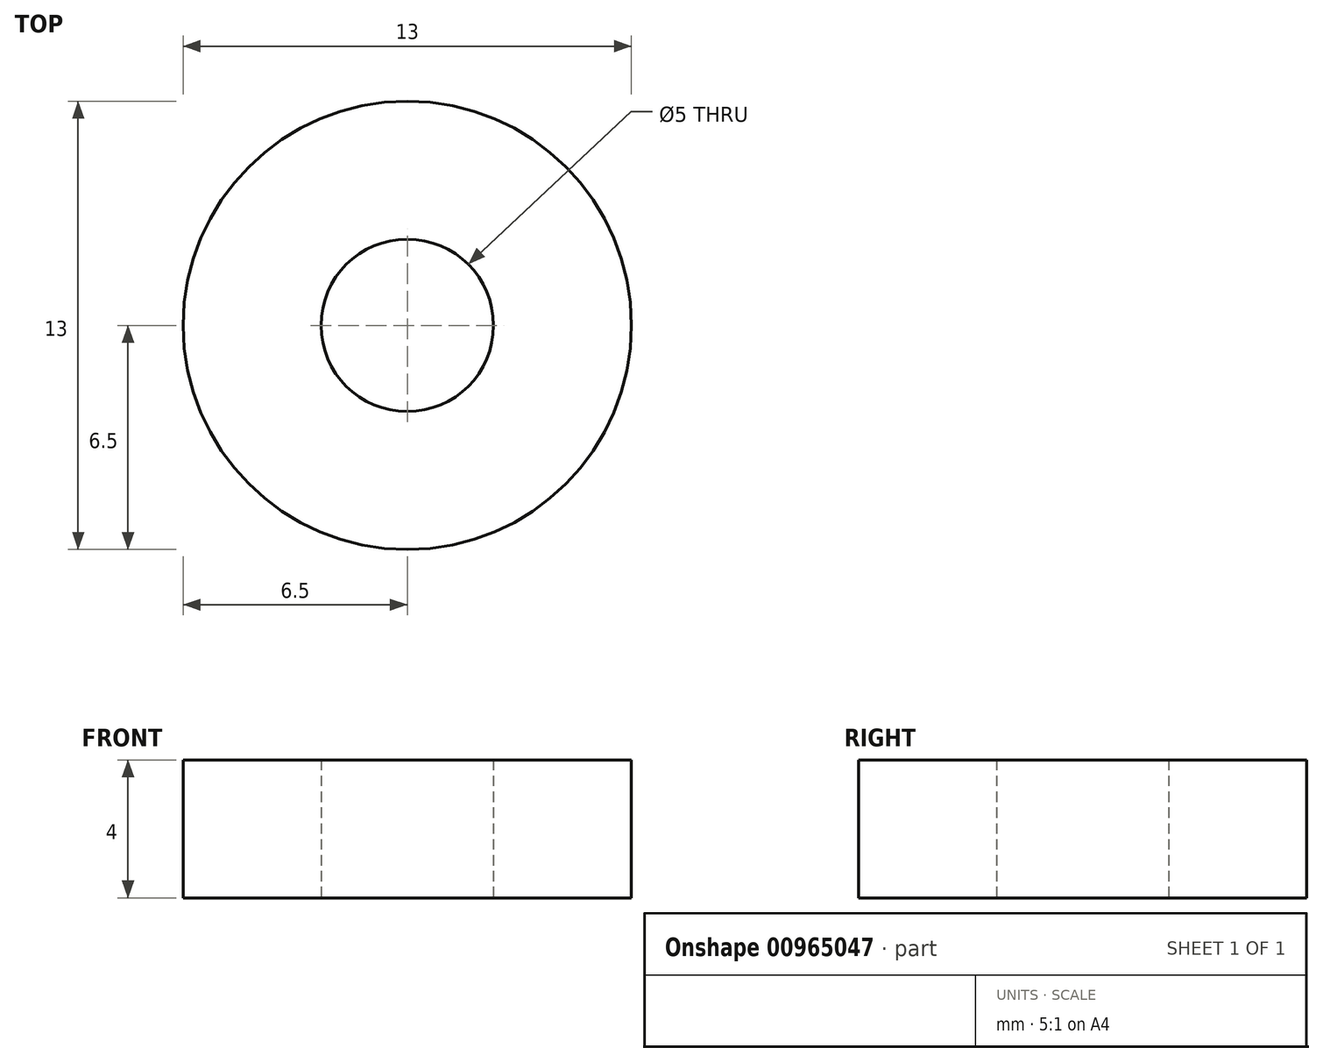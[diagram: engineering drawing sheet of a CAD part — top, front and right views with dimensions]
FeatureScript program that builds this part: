
annotation { "Feature Type Name" : "Feature", "Feature Type Description" : "" }
export const myFeature = defineFeature(function(context is Context, id is Id, definition is map)
    precondition{}
    {
        {
            var Q0;
            Q0=qCreatedBy(makeId("Top.planeOp"),FACE);
            var sketch = newSketch(context, id + "F0", { "sketchPlane" : qUnion([Q0])});
            skCircle(sketch, "E0", {"center": v(0, 0) * mm, "radius": 2.5 * mm});
            skCircle(sketch, "E1", {"center": v(0, 0) * mm, "radius": 6.5 * mm});
            skSolve(sketch);
        }
        {
            var Q0;
            Q0=makeQuery(id+"F0.imprint","IMPRINT",FACE,{"disambiguationData":[TD([[makeQuery(id+"F0.imprint","IMPRINT",EDGE,{"derivedFrom":sQuery(id+"F0.wireOp",EDGE,"E0")}),-1.0]])]});
            extrude(context, id + "F1", {"entities" : qUnion([Q0]), "depth" : 4 * mm, "offsetDistance" : 25 * mm});
        }
    });
